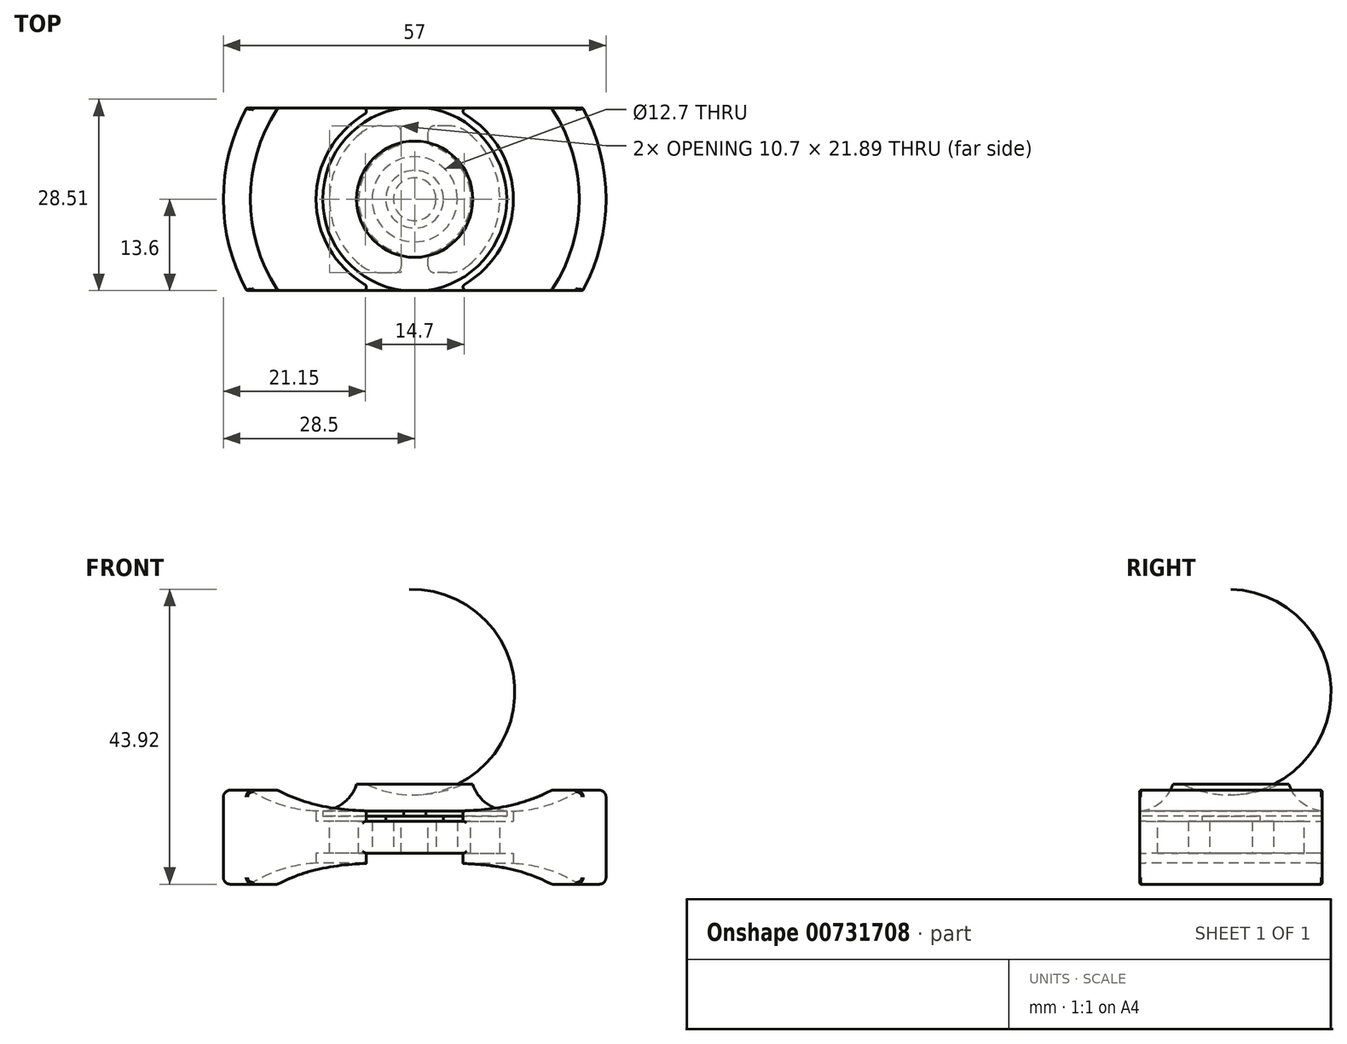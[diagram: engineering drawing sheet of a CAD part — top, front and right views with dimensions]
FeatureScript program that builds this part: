
annotation { "Feature Type Name" : "Feature", "Feature Type Description" : "" }
export const myFeature = defineFeature(function(context is Context, id is Id, definition is map)
    precondition{}
    {
        {
            var Q0;
            Q0=qCreatedBy(makeId("Front.planeOp"),FACE);
            var sketch = newSketch(context, id + "F0", { "sketchPlane" : qUnion([Q0])});
            skLineSegment(sketch, "E0", {"start": v(6.35, 0) * mm, "end": v(6.35, 4.76) * mm});
            skLineSegment(sketch, "E1", {"start": v(0, 6.26) * mm, "end": v(0, 11.13) * mm});
            skLineSegment(sketch, "E2", {"start": v(0, 19.9) * mm, "end": v(12.7, 19.9) * mm});
            skLineSegment(sketch, "E3", {"start": v(6.35, 4.76) * mm, "end": v(12.7, 4.76) * mm});
            skLineSegment(sketch, "E4", {"start": v(6.35, 0) * mm, "end": v(12.7, 0) * mm});
            skLineSegment(sketch, "E5", {"start": v(12.7, 4.76) * mm, "end": v(14.7, 4.76) * mm});
            skLineSegment(sketch, "E6", {"start": v(12.7, 0) * mm, "end": v(14.7, 0) * mm});
            skLineSegment(sketch, "E7", {"start": v(14.7, 4.76) * mm, "end": v(14.7, 6.26) * mm});
            skLineSegment(sketch, "E8", {"start": v(14.7, 0) * mm, "end": v(14.7, -1.5) * mm});
            skLineSegment(sketch, "E9", {"start": v(28.5, 2.38) * mm, "end": v(28.5, -4.62) * mm});
            skLineSegment(sketch, "E10", {"start": v(29.18, -4.62) * mm, "end": v(28.5, -4.62) * mm});
            skPoint(sketch, "E11.start.orphan", {"position": v(29.18, 11.38) * mm});
            skLineSegment(sketch, "E12", {"start": v(28.5, -4.62) * mm, "end": v(24.5, -4.62) * mm});
            skPoint(sketch, "E13.orphan", {"position": v(28.5, 13.95) * mm});
            skLineSegment(sketch, "E14", {"start": v(8.65, 12.63) * mm, "end": v(7.14, 12.63) * mm});
            skLineSegment(sketch, "E15", {"start": v(12.7, 6.26) * mm, "end": v(12.7, 6.26) * mm});
            skPoint(sketch, "E16.orphan", {"position": v(0, 12.63) * mm});
            skLineSegment(sketch, "E17", {"start": v(0, 0) * mm, "end": v(0, 4.76) * mm});
            skPoint(sketch, "E18.start.orphan", {"position": v(6.35, 2.38) * mm});
            skLineSegment(sketch, "E19", {"start": v(28.5, 2.38) * mm, "end": v(28.5, 9.38) * mm});
            skLineSegment(sketch, "E20", {"start": v(28.5, 9.38) * mm, "end": v(24.5, 9.38) * mm});
            skPoint(sketch, "E21.end.orphan", {"position": v(24.5, 11.13) * mm});
            skArc(sketch, "E22", {"start": v(14.7, 6.26) * mm, "mid": v(19.81, 7.16) * mm, "end": v(24.5, 9.38) * mm});
            skArc(sketch, "E23.MirrorCS", {"start": v(14.7, -1.5) * mm, "mid": v(19.81, -2.4) * mm, "end": v(24.5, -4.62) * mm});
            skPoint(sketch, "E24.start.orphan", {"position": v(25.51, 2.38) * mm});
            skLineSegment(sketch, "E25", {"start": v(0, 4.76) * mm, "end": v(0, 6.26) * mm});
            skPoint(sketch, "E26.startSnap0", {"position": v(0, 5.51) * mm});
            skLineSegment(sketch, "E27", {"start": v(8.65, 10.26) * mm, "end": v(7.14, 10.26) * mm});
            skPoint(sketch, "E28.orphan", {"position": v(8.65, 11.13) * mm});
            skPoint(sketch, "E29.start.orphan", {"position": v(8.65, 9.38) * mm});
            skArc(sketch, "E30", {"start": v(0, 8.7) * mm, "mid": v(3.66, 9.04) * mm, "end": v(7.14, 10.26) * mm});
            skLineSegment(sketch, "E31", {"start": v(12.7, 5.51) * mm, "end": v(4.3, 5.51) * mm});
            skLineSegment(sketch, "E32", {"start": v(12.7, 5.51) * mm, "end": v(13.7, 5.51) * mm});
            skPoint(sketch, "E32.endSnap0", {"position": v(13.7, 4.76) * mm});
            skLineSegment(sketch, "E33", {"start": v(13.7, 5.51) * mm, "end": v(13.7, 6.26) * mm});
            skArc(sketch, "E34", {"start": v(8.65, 10.26) * mm, "mid": v(10.58, 7.5) * mm, "end": v(13.7, 6.26) * mm});
            skLineSegment(sketch, "E35.MirrorCS", {"start": v(12.7, -0.75) * mm, "end": v(0, -0.75) * mm});
            skArc(sketch, "E36.MirrorCS", {"start": v(0, -3.93) * mm, "mid": v(3.66, -4.28) * mm, "end": v(7.14, -5.5) * mm});
            skArc(sketch, "E37.MirrorCS", {"start": v(8.65, -5.5) * mm, "mid": v(10.58, -2.74) * mm, "end": v(13.7, -1.5) * mm});
            skLineSegment(sketch, "E38", {"start": v(13.7, -1.5) * mm, "end": v(13.7, -0.75) * mm});
            skLineSegment(sketch, "E39", {"start": v(13.7, -0.75) * mm, "end": v(12.7, -0.75) * mm});
            skLineSegment(sketch, "E40", {"start": v(0, -3.93) * mm, "end": v(0, -0.75) * mm});
            skLineSegment(sketch, "E41", {"start": v(7.14, -5.5) * mm, "end": v(8.65, -5.5) * mm});
            skLineSegment(sketch, "E42.top", {"start": v(0, 0) * mm, "end": v(3.18, 0) * mm});
            skLineSegment(sketch, "E42.left", {"start": v(0, 5.51) * mm, "end": v(0, 0) * mm});
            skLineSegment(sketch, "E42.right", {"start": v(3.18, 4.76) * mm, "end": v(3.18, 0) * mm});
            skPoint(sketch, "E43.end.orphan", {"position": v(3.18, 2.38) * mm});
            skPoint(sketch, "E43.start.orphan", {"position": v(4.3, 2.38) * mm});
            skLineSegment(sketch, "E44.top", {"start": v(3.18, 4.76) * mm, "end": v(4.3, 4.76) * mm});
            skLineSegment(sketch, "E44.right", {"start": v(4.3, 5.51) * mm, "end": v(4.3, 4.76) * mm});
            skSolve(sketch);
        }
        {
            var Q0;
            Q0=makeQuery(id+"F0.imprint","IMPRINT",FACE,{"disambiguationData":[TD([[makeQuery(id+"F0.imprint","IMPRINT",EDGE,{"derivedFrom":sQuery(id+"F0.wireOp",EDGE,"E0")}),-1.0]])]});
            var Q1;
            Q1=makeQuery(id+"F0.imprint","IMPRINT",FACE,{"disambiguationData":[TD([[makeQuery(id+"F0.imprint","IMPRINT",EDGE,{"derivedFrom":sQuery(id+"F0.wireOp",EDGE,"E27")}),1.0]])]});
            var Q2;
            Q2=makeQuery(id+"F0.imprint","IMPRINT",FACE,{"disambiguationData":[TD([[makeQuery(id+"F0.imprint","IMPRINT",EDGE,{"derivedFrom":sQuery(id+"F0.wireOp",EDGE,"E36.MirrorCS")}),1.0]])]});
            var Q3;
            Q3=sQuery(id+"F0.wireOp",EDGE,"E17");
            revolve(context, id + "F1", {"surfaceOperationType" : NewSurfaceOperationType.NEW, "entities" : qUnion([Q0, Q1, Q2]), "axis" : qUnion([Q3]), "revolveType" : RevolveType.FULL});
        }
        {
            var Q0;
            Q0=qCreatedBy(makeId("Top.planeOp"),FACE);
            var sketch = newSketch(context, id + "F2", { "sketchPlane" : qUnion([Q0])});
            skPoint(sketch, "E45.middle", {"position": v(0, 0) * mm});
            skLineSegment(sketch, "E46", {"start": v(0, 0) * mm, "end": v(35.85, 0) * mm});
            skPoint(sketch, "E46.endSnap0", {"position": v(13.6, 0) * mm});
            skLineSegment(sketch, "E47", {"start": v(35.85, 0) * mm, "end": v(-25.76, 0) * mm});
            skPoint(sketch, "E48.center.orphan", {"position": v(0, 38.74) * mm});
            skPoint(sketch, "E49.orphan", {"position": v(13.6, 13.6) * mm});
            skPoint(sketch, "E50.orphan", {"position": v(-13.6, 13.6) * mm});
            skPoint(sketch, "E45.top.start.orphan", {"position": v(13.6, -13.6) * mm});
            skPoint(sketch, "E45.right.end.orphan", {"position": v(-13.6, -13.6) * mm});
            skLineSegment(sketch, "E51.bottom", {"start": v(13.6, -13.6) * mm, "end": v(-13.6, -13.6) * mm});
            skLineSegment(sketch, "E51.top", {"start": v(13.6, 13.6) * mm, "end": v(-13.6, 13.6) * mm});
            skLineSegment(sketch, "E51.left", {"start": v(13.6, -13.6) * mm, "end": v(13.6, 13.6) * mm});
            skLineSegment(sketch, "E51.right", {"start": v(-13.6, -13.6) * mm, "end": v(-13.6, 13.6) * mm});
            skLineSegment(sketch, "E52.bottom", {"start": v(-13.6, -13.6) * mm, "end": v(13.6, -13.6) * mm});
            skLineSegment(sketch, "E53.bottom", {"start": v(-13.6, 13.6) * mm, "end": v(13.6, 13.6) * mm});
            skPoint(sketch, "E53.left.start.orphan", {"position": v(-35.02, 13.6) * mm});
            skPoint(sketch, "E54.orphan", {"position": v(-34.53, -13.6) * mm});
            skLineSegment(sketch, "E55.bottom", {"start": v(-29.3, 13.6) * mm, "end": v(32.8, 13.6) * mm});
            skLineSegment(sketch, "E55.top", {"start": v(-29.3, 33.2) * mm, "end": v(32.8, 33.2) * mm});
            skLineSegment(sketch, "E55.left", {"start": v(-29.3, 13.6) * mm, "end": v(-29.3, 33.2) * mm});
            skLineSegment(sketch, "E55.right", {"start": v(32.8, 13.6) * mm, "end": v(32.8, 33.2) * mm});
            skLineSegment(sketch, "E56.bottom", {"start": v(34.26, -13.6) * mm, "end": v(-29.18, -13.6) * mm});
            skLineSegment(sketch, "E56.top", {"start": v(34.26, -33.7) * mm, "end": v(-29.18, -33.7) * mm});
            skLineSegment(sketch, "E56.left", {"start": v(34.26, -13.6) * mm, "end": v(34.26, -33.7) * mm});
            skLineSegment(sketch, "E56.right", {"start": v(-29.18, -13.6) * mm, "end": v(-29.18, -33.7) * mm});
            skSolve(sketch);
        }
        {
            var Q0;
            Q0=makeQuery(id+"F2.imprint","IMPRINT",FACE,{"disambiguationData":[TD([[makeQuery(id+"F2.imprint","IMPRINT",EDGE,{"derivedFrom":sQuery(id+"F2.wireOp",EDGE,"E56.top")}),-1.0]])]});
            var Q1;
            Q1=makeQuery(id+"F2.imprint","IMPRINT",FACE,{"disambiguationData":[TD([[makeQuery(id+"F2.imprint","IMPRINT",EDGE,{"derivedFrom":sQuery(id+"F2.wireOp",EDGE,"E55.top")}),-1.0]])]});
            extrude(context, id + "F3", {"entities" : qUnion([Q0, Q1]), "operationType" : NewBodyOperationType.REMOVE, "endBound" : BoundingType.SYMMETRIC, "oppositeDirection" : true, "depth" : 25 * mm, "offsetDistance" : 25 * mm});
        }
        {
            var Q0;
            Q0=makeQuery(id+"F3.boolean.opBoolean","SPLIT",EDGE,{"disambiguationData":[OD(0.0)],"derivedFrom":makeQuery(id+"F1.opRevolve","SWEPT_EDGE",EDGE,{"disambiguationData":[OSD([sQuery(id+"F0.wireOp",EDGE,"E9"),sQuery(id+"F0.wireOp",EDGE,"E12")])]})});
            var Q1;
            Q1=makeQuery(id+"F3.boolean.opBoolean","SPLIT",EDGE,{"disambiguationData":[OD(1.0)],"derivedFrom":makeQuery(id+"F1.opRevolve","SWEPT_EDGE",EDGE,{"disambiguationData":[OSD([sQuery(id+"F0.wireOp",EDGE,"E9"),sQuery(id+"F0.wireOp",EDGE,"E12")])]})});
            var Q2;
            Q2=makeQuery(id+"F3.boolean.opBoolean","SPLIT",EDGE,{"disambiguationData":[OD(1.0)],"derivedFrom":makeQuery(id+"F1.opRevolve","SWEPT_EDGE",EDGE,{"disambiguationData":[OSD([sQuery(id+"F0.wireOp",EDGE,"E19"),sQuery(id+"F0.wireOp",EDGE,"E20")])]})});
            var Q3;
            Q3=makeQuery(id+"F3.boolean.opBoolean","SPLIT",EDGE,{"disambiguationData":[OD(0.0)],"derivedFrom":makeQuery(id+"F1.opRevolve","SWEPT_EDGE",EDGE,{"disambiguationData":[OSD([sQuery(id+"F0.wireOp",EDGE,"E19"),sQuery(id+"F0.wireOp",EDGE,"E20")])]})});
            fillet(context, id + "F4", {"entities" : qUnion([Q0, Q1, Q2, Q3]), "radius" : 1 * mm, "tangentPropagation" : true, "allowEdgeOverflow" : false});
        }
        {
            var Q0;
            Q0=makeQuery(id+"F3.boolean.opBoolean","INTERSECT",EDGE,{"disambiguationData":[OD(0.0)],"derivedFrom":[makeQuery(id+"F1.opRevolve","SWEPT_FACE",FACE,{"disambiguationData":[OSD([sQuery(id+"F0.wireOp",EDGE,"E8")])]}),makeQuery(id+"F3.opExtrude","SWEPT_FACE",FACE,{"disambiguationData":[OSD([sQuery(id+"F2.wireOp",EDGE,"E55.bottom")])]})]});
            var Q1;
            Q1=makeQuery(id+"F3.boolean.opBoolean","INTERSECT",EDGE,{"disambiguationData":[OD(0.0)],"derivedFrom":[makeQuery(id+"F1.opRevolve","SWEPT_FACE",FACE,{"disambiguationData":[OSD([sQuery(id+"F0.wireOp",EDGE,"E7")])]}),makeQuery(id+"F3.opExtrude","SWEPT_FACE",FACE,{"disambiguationData":[OSD([sQuery(id+"F2.wireOp",EDGE,"E55.bottom")])]})]});
            var Q2;
            Q2=makeQuery(id+"F3.boolean.opBoolean","INTERSECT",EDGE,{"disambiguationData":[OD(1.0)],"derivedFrom":[makeQuery(id+"F1.opRevolve","SWEPT_FACE",FACE,{"disambiguationData":[OSD([sQuery(id+"F0.wireOp",EDGE,"E8")])]}),makeQuery(id+"F3.opExtrude","SWEPT_FACE",FACE,{"disambiguationData":[OSD([sQuery(id+"F2.wireOp",EDGE,"E55.bottom")])]})]});
            var Q3;
            Q3=makeQuery(id+"F3.boolean.opBoolean","INTERSECT",EDGE,{"disambiguationData":[OD(1.0)],"derivedFrom":[makeQuery(id+"F1.opRevolve","SWEPT_FACE",FACE,{"disambiguationData":[OSD([sQuery(id+"F0.wireOp",EDGE,"E7")])]}),makeQuery(id+"F3.opExtrude","SWEPT_FACE",FACE,{"disambiguationData":[OSD([sQuery(id+"F2.wireOp",EDGE,"E55.bottom")])]})]});
            var Q4;
            Q4=makeQuery(id+"F3.boolean.opBoolean","INTERSECT",EDGE,{"disambiguationData":[OD(0.0)],"derivedFrom":[makeQuery(id+"F1.opRevolve","SWEPT_FACE",FACE,{"disambiguationData":[OSD([sQuery(id+"F0.wireOp",EDGE,"E8")])]}),makeQuery(id+"F3.opExtrude","SWEPT_FACE",FACE,{"disambiguationData":[OSD([sQuery(id+"F2.wireOp",EDGE,"E56.bottom")])]})]});
            var Q5;
            Q5=makeQuery(id+"F3.boolean.opBoolean","INTERSECT",EDGE,{"disambiguationData":[OD(0.0)],"derivedFrom":[makeQuery(id+"F1.opRevolve","SWEPT_FACE",FACE,{"disambiguationData":[OSD([sQuery(id+"F0.wireOp",EDGE,"E7")])]}),makeQuery(id+"F3.opExtrude","SWEPT_FACE",FACE,{"disambiguationData":[OSD([sQuery(id+"F2.wireOp",EDGE,"E56.bottom")])]})]});
            var Q6;
            Q6=makeQuery(id+"F3.boolean.opBoolean","INTERSECT",EDGE,{"disambiguationData":[OD(1.0)],"derivedFrom":[makeQuery(id+"F1.opRevolve","SWEPT_FACE",FACE,{"disambiguationData":[OSD([sQuery(id+"F0.wireOp",EDGE,"E8")])]}),makeQuery(id+"F3.opExtrude","SWEPT_FACE",FACE,{"disambiguationData":[OSD([sQuery(id+"F2.wireOp",EDGE,"E56.bottom")])]})]});
            var Q7;
            Q7=makeQuery(id+"F3.boolean.opBoolean","INTERSECT",EDGE,{"disambiguationData":[OD(1.0)],"derivedFrom":[makeQuery(id+"F1.opRevolve","SWEPT_FACE",FACE,{"disambiguationData":[OSD([sQuery(id+"F0.wireOp",EDGE,"E7")])]}),makeQuery(id+"F3.opExtrude","SWEPT_FACE",FACE,{"disambiguationData":[OSD([sQuery(id+"F2.wireOp",EDGE,"E56.bottom")])]})]});
            fillet(context, id + "F5", {"entities" : qUnion([Q0, Q1, Q2, Q3, Q4, Q5, Q6, Q7]), "radius" : .5 * mm, "tangentPropagation" : true, "allowEdgeOverflow" : false});
        }
        {
            var Q0;
            Q0=makeQuery(id+"F3.boolean.opBoolean","INTERSECT",EDGE,{"disambiguationData":[OD(1.0)],"derivedFrom":[makeQuery(id+"F1.opRevolve","SWEPT_FACE",FACE,{"disambiguationData":[OSD([sQuery(id+"F0.wireOp",EDGE,"E9"),sQuery(id+"F0.wireOp",EDGE,"E19")])]}),makeQuery(id+"F3.opExtrude","SWEPT_FACE",FACE,{"disambiguationData":[OSD([sQuery(id+"F2.wireOp",EDGE,"E56.bottom")])]})]});
            var Q1;
            Q1=makeQuery(id+"F3.boolean.opBoolean","INTERSECT",EDGE,{"disambiguationData":[OD(0.0)],"derivedFrom":[makeQuery(id+"F1.opRevolve","SWEPT_FACE",FACE,{"disambiguationData":[OSD([sQuery(id+"F0.wireOp",EDGE,"E9"),sQuery(id+"F0.wireOp",EDGE,"E19")])]}),makeQuery(id+"F3.opExtrude","SWEPT_FACE",FACE,{"disambiguationData":[OSD([sQuery(id+"F2.wireOp",EDGE,"E55.bottom")])]})]});
            var Q2;
            Q2=makeQuery(id+"F3.boolean.opBoolean","INTERSECT",EDGE,{"disambiguationData":[OD(1.0)],"derivedFrom":[makeQuery(id+"F1.opRevolve","SWEPT_FACE",FACE,{"disambiguationData":[OSD([sQuery(id+"F0.wireOp",EDGE,"E9"),sQuery(id+"F0.wireOp",EDGE,"E19")])]}),makeQuery(id+"F3.opExtrude","SWEPT_FACE",FACE,{"disambiguationData":[OSD([sQuery(id+"F2.wireOp",EDGE,"E55.bottom")])]})]});
            var Q3;
            Q3=makeQuery(id+"F3.boolean.opBoolean","INTERSECT",EDGE,{"disambiguationData":[OD(0.0)],"derivedFrom":[makeQuery(id+"F1.opRevolve","SWEPT_FACE",FACE,{"disambiguationData":[OSD([sQuery(id+"F0.wireOp",EDGE,"E9"),sQuery(id+"F0.wireOp",EDGE,"E19")])]}),makeQuery(id+"F3.opExtrude","SWEPT_FACE",FACE,{"disambiguationData":[OSD([sQuery(id+"F2.wireOp",EDGE,"E56.bottom")])]})]});
            var Q4;
            Q4=makeQuery(id+"F3.boolean.opBoolean","INTERSECT",EDGE,{"derivedFrom":[makeQuery(id+"F1.opRevolve","SWEPT_FACE",FACE,{"disambiguationData":[OSD([sQuery(id+"F0.wireOp",EDGE,"E4"),sQuery(id+"F0.wireOp",EDGE,"E6")])]}),makeQuery(id+"F3.opExtrude","SWEPT_FACE",FACE,{"disambiguationData":[OSD([sQuery(id+"F2.wireOp",EDGE,"E56.bottom")])]})]});
            var Q5;
            Q5=makeQuery(id+"F3.boolean.opBoolean","INTERSECT",EDGE,{"derivedFrom":[makeQuery(id+"F1.opRevolve","SWEPT_FACE",FACE,{"disambiguationData":[OSD([sQuery(id+"F0.wireOp",EDGE,"E3"),sQuery(id+"F0.wireOp",EDGE,"E5")])]}),makeQuery(id+"F3.opExtrude","SWEPT_FACE",FACE,{"disambiguationData":[OSD([sQuery(id+"F2.wireOp",EDGE,"E56.bottom")])]})]});
            var Q6;
            Q6=makeQuery(id+"F3.boolean.opBoolean","INTERSECT",EDGE,{"derivedFrom":[makeQuery(id+"F1.opRevolve","SWEPT_FACE",FACE,{"disambiguationData":[OSD([sQuery(id+"F0.wireOp",EDGE,"E4"),sQuery(id+"F0.wireOp",EDGE,"E6")])]}),makeQuery(id+"F3.opExtrude","SWEPT_FACE",FACE,{"disambiguationData":[OSD([sQuery(id+"F2.wireOp",EDGE,"E55.bottom")])]})]});
            var Q7;
            Q7=makeQuery(id+"F3.boolean.opBoolean","INTERSECT",EDGE,{"derivedFrom":[makeQuery(id+"F1.opRevolve","SWEPT_FACE",FACE,{"disambiguationData":[OSD([sQuery(id+"F0.wireOp",EDGE,"E3"),sQuery(id+"F0.wireOp",EDGE,"E5")])]}),makeQuery(id+"F3.opExtrude","SWEPT_FACE",FACE,{"disambiguationData":[OSD([sQuery(id+"F2.wireOp",EDGE,"E55.bottom")])]})]});
            var Q8;
            Q8=makeQuery(id+"F1.opRevolve","SWEPT_EDGE",EDGE,{"disambiguationData":[OSD([sQuery(id+"F0.wireOp",EDGE,"E36.MirrorCS"),sQuery(id+"F0.wireOp",EDGE,"E41")])]});
            fillet(context, id + "F6", {"entities" : qUnion([Q0, Q1, Q2, Q3, Q4, Q5, Q6, Q7, Q8]), "radius" : .25 * mm, "tangentPropagation" : true, "allowEdgeOverflow" : false});
        }
        {
            var Q0;
            Q0=makeQuery(id+"F1.opRevolve","SWEPT_FACE",FACE,{"disambiguationData":[OSD([sQuery(id+"F0.wireOp",EDGE,"E3"),sQuery(id+"F0.wireOp",EDGE,"E5")])]});
            var sketch = newSketch(context, id + "F7", { "sketchPlane" : qUnion([Q0])});
            skLineSegment(sketch, "E57", {"start": v(0, 6.35) * mm, "end": v(0, 8.35) * mm});
            skLineSegment(sketch, "E58", {"start": v(0, -6.35) * mm, "end": v(0, -13.35) * mm});
            skPoint(sketch, "E58.startSnap0", {"position": v(0, -13.35) * mm});
            skArc(sketch, "E59.0", {"start": v(-6.44, -10.95) * mm, "mid": v(-12.7, 0) * mm, "end": v(-6.44, 10.95) * mm});
            skLineSegment(sketch, "E60.0", {"start": v(-2, -8.1) * mm, "end": v(-2, -10.95) * mm});
            skLineSegment(sketch, "E61.0", {"start": v(-2, 8.1) * mm, "end": v(-2, 10.95) * mm});
            skArc(sketch, "E62.0", {"start": v(-2, 8.1) * mm, "mid": v(-8.35, 0) * mm, "end": v(-2, -8.1) * mm});
            skLineSegment(sketch, "E63", {"start": v(-6.44, 10.95) * mm, "end": v(-2, 10.95) * mm});
            skLineSegment(sketch, "E64", {"start": v(-6.44, -10.95) * mm, "end": v(-2, -10.95) * mm});
            skPoint(sketch, "E64.endSnap0", {"position": v(-2, -9.85) * mm});
            skPoint(sketch, "E65.orphan", {"position": v(0, 13.35) * mm});
            skPoint(sketch, "E66.orphan", {"position": v(-2, -6.35) * mm});
            skPoint(sketch, "E67.orphan", {"position": v(-2, -13.35) * mm});
            skArc(sketch, "E68.MirrorCS", {"start": v(6.44, -10.95) * mm, "mid": v(12.7, 0) * mm, "end": v(6.44, 10.95) * mm});
            skLineSegment(sketch, "E69.MirrorCS", {"start": v(6.44, -10.95) * mm, "end": v(2, -10.95) * mm});
            skArc(sketch, "E70.MirrorCS", {"start": v(2, 8.1) * mm, "mid": v(8.35, 0) * mm, "end": v(2, -8.1) * mm});
            skLineSegment(sketch, "E71.MirrorCS", {"start": v(2, 8.1) * mm, "end": v(2, 10.95) * mm});
            skLineSegment(sketch, "E72.MirrorCS", {"start": v(6.44, 10.95) * mm, "end": v(2, 10.95) * mm});
            skLineSegment(sketch, "E73", {"start": v(2, -10.95) * mm, "end": v(2, -8.1) * mm});
            skSolve(sketch);
        }
        {
            var Q0;
            Q0 = qSketchRegion(id + "F7", true);
            extrude(context, id + "F8", {"entities" : qUnion([Q0]), "operationType" : NewBodyOperationType.REMOVE, "oppositeDirection" : true, "depth" : 25 * mm, "offsetDistance" : 25 * mm});
        }
        {
            var Q0;
            Q0=makeQuery(id+"F8.boolean.opBoolean","COPY",EDGE,{"derivedFrom":makeQuery(id+"F8.opExtrude","SWEPT_EDGE",EDGE,{"disambiguationData":[OSD([sQuery(id+"F7.wireOp",EDGE,"E68.MirrorCS"),sQuery(id+"F7.wireOp",EDGE,"E72.MirrorCS")])]})});
            var Q1;
            Q1=makeQuery(id+"F8.boolean.opBoolean","COPY",EDGE,{"derivedFrom":makeQuery(id+"F8.opExtrude","SWEPT_EDGE",EDGE,{"disambiguationData":[OSD([sQuery(id+"F7.wireOp",EDGE,"E59.0"),sQuery(id+"F7.wireOp",EDGE,"E63")])]})});
            var Q2;
            Q2=makeQuery(id+"F8.boolean.opBoolean","COPY",EDGE,{"derivedFrom":makeQuery(id+"F8.opExtrude","SWEPT_EDGE",EDGE,{"disambiguationData":[OSD([sQuery(id+"F7.wireOp",EDGE,"E59.0"),sQuery(id+"F7.wireOp",EDGE,"E64")])]})});
            var Q3;
            Q3=makeQuery(id+"F8.boolean.opBoolean","COPY",EDGE,{"derivedFrom":makeQuery(id+"F8.opExtrude","SWEPT_EDGE",EDGE,{"disambiguationData":[OSD([sQuery(id+"F7.wireOp",EDGE,"E68.MirrorCS"),sQuery(id+"F7.wireOp",EDGE,"E69.MirrorCS")])]})});
            fillet(context, id + "F9", {"entities" : qUnion([Q0, Q1, Q2, Q3]), "radius" : 5 * mm, "tangentPropagation" : true, "allowEdgeOverflow" : false});
        }
        {
            var Q0;
            Q0=makeQuery(id+"F8.boolean.opBoolean","COPY",EDGE,{"derivedFrom":makeQuery(id+"F8.opExtrude","SWEPT_EDGE",EDGE,{"disambiguationData":[OSD([sQuery(id+"F7.wireOp",EDGE,"E61.0"),sQuery(id+"F7.wireOp",EDGE,"E63")])]})});
            var Q1;
            Q1=makeQuery(id+"F8.boolean.opBoolean","COPY",EDGE,{"derivedFrom":makeQuery(id+"F8.opExtrude","SWEPT_EDGE",EDGE,{"disambiguationData":[OSD([sQuery(id+"F7.wireOp",EDGE,"E70.MirrorCS"),sQuery(id+"F7.wireOp",EDGE,"E71.MirrorCS")])]})});
            var Q2;
            Q2=makeQuery(id+"F8.boolean.opBoolean","COPY",EDGE,{"derivedFrom":makeQuery(id+"F8.opExtrude","SWEPT_EDGE",EDGE,{"disambiguationData":[OSD([sQuery(id+"F7.wireOp",EDGE,"E69.MirrorCS"),sQuery(id+"F7.wireOp",EDGE,"E73")])]})});
            var Q3;
            Q3=makeQuery(id+"F8.boolean.opBoolean","COPY",EDGE,{"derivedFrom":makeQuery(id+"F8.opExtrude","SWEPT_EDGE",EDGE,{"disambiguationData":[OSD([sQuery(id+"F7.wireOp",EDGE,"E61.0"),sQuery(id+"F7.wireOp",EDGE,"E62.0")])]})});
            var Q4;
            Q4=makeQuery(id+"F8.boolean.opBoolean","COPY",EDGE,{"derivedFrom":makeQuery(id+"F8.opExtrude","SWEPT_EDGE",EDGE,{"disambiguationData":[OSD([sQuery(id+"F7.wireOp",EDGE,"E71.MirrorCS"),sQuery(id+"F7.wireOp",EDGE,"E72.MirrorCS")])]})});
            var Q5;
            Q5=makeQuery(id+"F8.boolean.opBoolean","COPY",EDGE,{"derivedFrom":makeQuery(id+"F8.opExtrude","SWEPT_EDGE",EDGE,{"disambiguationData":[OSD([sQuery(id+"F7.wireOp",EDGE,"E70.MirrorCS"),sQuery(id+"F7.wireOp",EDGE,"E73")])]})});
            var Q6;
            Q6=makeQuery(id+"F8.boolean.opBoolean","COPY",EDGE,{"derivedFrom":makeQuery(id+"F8.opExtrude","SWEPT_EDGE",EDGE,{"disambiguationData":[OSD([sQuery(id+"F7.wireOp",EDGE,"E60.0"),sQuery(id+"F7.wireOp",EDGE,"E64")])]})});
            var Q7;
            Q7=makeQuery(id+"F8.boolean.opBoolean","COPY",EDGE,{"derivedFrom":makeQuery(id+"F8.opExtrude","SWEPT_EDGE",EDGE,{"disambiguationData":[OSD([sQuery(id+"F7.wireOp",EDGE,"E60.0"),sQuery(id+"F7.wireOp",EDGE,"E62.0")])]})});
            fillet(context, id + "F10", {"entities" : qUnion([Q0, Q1, Q2, Q3, Q4, Q5, Q6, Q7]), "radius" : 1 * mm, "tangentPropagation" : true, "allowEdgeOverflow" : false});
        }
        {
            var Q0;
            Q0=makeQuery(id+"F1.opRevolve","SWEPT_EDGE",EDGE,{"disambiguationData":[OSD([sQuery(id+"F0.wireOp",EDGE,"E27"),sQuery(id+"F0.wireOp",EDGE,"E30")])]});
            fillet(context, id + "F11", {"entities" : qUnion([Q0]), "radius" : .25 * mm, "tangentPropagation" : true, "allowEdgeOverflow" : false});
        }
    });
